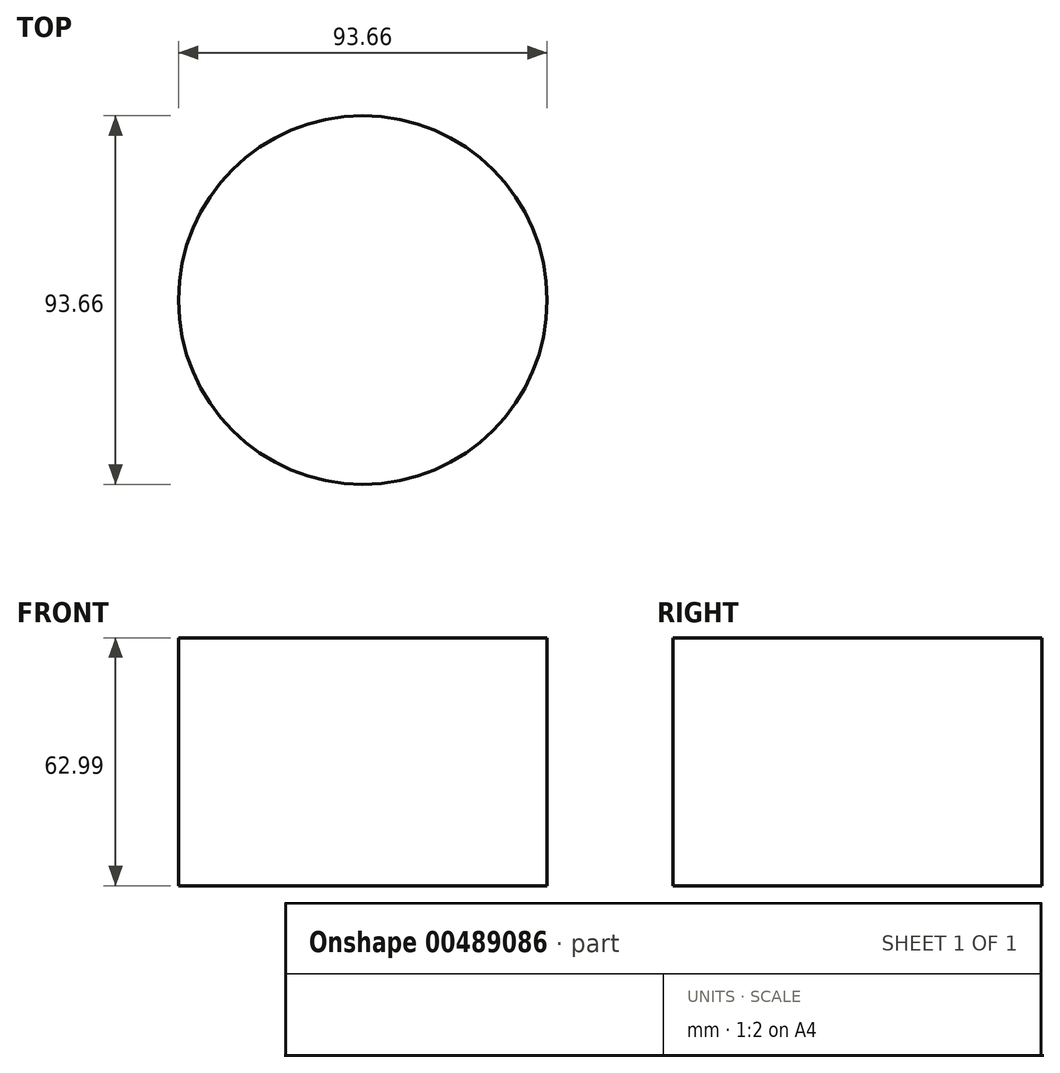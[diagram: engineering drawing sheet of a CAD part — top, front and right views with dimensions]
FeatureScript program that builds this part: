
annotation { "Feature Type Name" : "Feature", "Feature Type Description" : "" }
export const myFeature = defineFeature(function(context is Context, id is Id, definition is map)
    precondition{}
    {
        {
            var Q0;
            Q0=qCreatedBy(makeId("Top.planeOp"),FACE);
            var sketch = newSketch(context, id + "F0", { "sketchPlane" : qUnion([Q0])});
            skCircle(sketch, "E0", {"center": v(0, 0) * mm, "radius": 46.83 * mm});
            skSolve(sketch);
        }
        {
            var Q0;
            Q0=sQuery(id+"F0.wireOp",EDGE,"E0");
            extrude(context, id + "F1", {"bodyType" : ToolBodyType.SURFACE, "surfaceEntities" : qUnion([Q0]), "depth" : 63 * mm});
        }
    });
